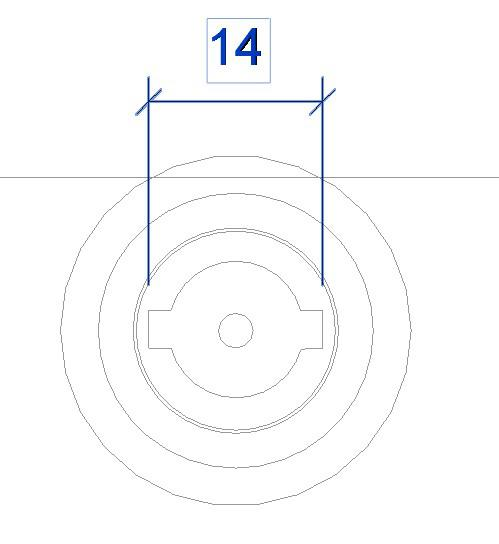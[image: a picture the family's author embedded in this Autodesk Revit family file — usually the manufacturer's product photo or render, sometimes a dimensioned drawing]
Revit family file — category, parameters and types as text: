
# Revit family: AquaMaster-Inverter-P_RFA-2022
name_source: partatom
category: Mechanické zařízení
units: mm (PartAtom-declared; Revit-internal decimal feet)

## family parameters
Bod výpočtu místnosti = Ne
Kóta kulaté spojky = Použít průměr
Nadpis OmniClass = Climate Control (HVAC)
Ořezat dutým tvarem při načtení = Ne
Sdílené = Ne
Typ dílu = Normální
Vždy vertikální = Ano
Zachovat orientaci poznámky = Ne
Založené na pracovní rovině = Ne
Číslo OmniClass = 23.75.00.00

## types (5) — shared parameters
CI_otopná voda – vstup = 1'' (vnější)
CO_otopná voda – výstup = 1'' (vnější)
MT_CI diameter = 28 mm  [stored 0.0918635 ft]
MT_CO diameter = 28 mm  [stored 0.0918635 ft]
MT_EC1 offset_X = 25 mm  [stored 0.082021 ft]
MT_active power = 0 W
MT_angle length_X = 406 mm  [stored 1.33202 ft]
MT_angle offset = 60 mm  [stored 0.19685 ft]
MT_apparent power = 0 VA
MT_case mat = MT_RAL7016
MT_case width = 526 mm  [stored 1.72572 ft]
MT_clearance back = 200 mm  [stored 0.656168 ft]
MT_clearance front = 600 mm
MT_cover front_X = 446 mm  [stored 1.46325 ft]
MT_cover top_X = 446 mm  [stored 1.46325 ft]
MT_frekvence (Hz) = 50 Hz
MT_ground height = 30 mm  [stored 0.0984252 ft]
MT_pipe connector mat = MT_RGB-130-130-130
MT_pipe mat = MT_angle-corner
Popis = Tepelné čerpadlo země/voda (R290)
URL = https://www.mastertherm.cz
Výrobce = Master Therm
zero-valued in all types: Cena, MT_CosPhi, Výchozí výška

## per-type parameters (varying)
- AQ45IP: EI_kolektor – vstup=5/4'' (vnější); EO_kolektor – výstup=5/4'' (vnější); Elektropřipojení=2xPG16; 4xPG13.5; Komentáře k typům=KOMPRESOR: BLDC Inverter; 15 – 120 rps; olej – (HAF68D1U) – 2.0 l; max. prov. proud – 24 A; VÝPARNÍK: deskový (nerez.); AISI316; průtok vody (W/W) – 2.14 kg/s; min. průtok – 1.61 kg/s; průtok směsi (B/W) – 1.04 kg/s; min. průtok – 0.63 kg/s; teplotní rozdíl – 3 K; vnitřní objem – 5.1 l; ext. tlak čerpadla – 15 m; max. příkon čerpadla – 400 W; KONDENZÁTOR: deskový (nerez.); AISI316; průtok otopné vody – 0.7 kg/s; min. průtok – 0.53 kg/s; teplotní rozdíl – 5 K; vnitřní objem – 4.1 l; ext. tlak čerpadla – 8.0 m; max. příkon čerpadla – 200 W; CHL. OKRUH: R290 (0.9 kg); EK (volitelně): není k dispozici; REGULACE: regulátor – pCO5; EEV – ano; čidlo otopné vody – ano; čidlo mix – ano (2x); čidlo TUV – ano; ext. čidlo – ano; ekviterm. reg. – ano; chladivo – 2xPT; ESI: 3x400 V; 50 Hz; max. proud – 25 A; ROZMĚRY: otopná voda, směs – 1", 5/4" (vnější); 120x53x72 cm; 180 kg; LIMITNÍ PROVOZNÍ PARAMETRY: max. přetlak vody – 0.25 MPa; max. přetlak chladiva – 3.1 MPa; směs min./max.: -5/+20 °C; voda min./max.: 20/75 °C; MT_CI offset_X=73 mm  [stored 0.239501 ft]; MT_CO offset_X=173 mm  [stored 0.567585 ft]; MT_EC1 offset_Y=90 mm; MT_EC2 offset_X=25 mm  [stored 0.082021 ft]; MT_EC2 offset_Y=60 mm  [stored 0.19685 ft]; MT_EC3 offset_X=25 mm  [stored 0.082021 ft]; MT_EC3 offset_Y=30 mm  [stored 0.0984252 ft]; MT_EC4 offset_X=421 mm  [stored 1.38123 ft]; MT_EC4 offset_Y=90 mm; MT_EC5 offset_X=421 mm  [stored 1.38123 ft]; MT_EC5 offset_Y=60 mm  [stored 0.19685 ft]; MT_EC5-EC6_YES=Ano; MT_EC6 offset_X=421 mm  [stored 1.38123 ft]; MT_EC6 offset_Y=30 mm  [stored 0.0984252 ft]; MT_EI diameter=35 mm  [stored 0.114829 ft]; MT_EI offset_X=373 mm  [stored 1.22375 ft]; MT_EO diameter=35 mm  [stored 0.114829 ft]; MT_EO offset_X=273 mm  [stored 0.895669 ft]; MT_TYPE=45; MT_angle length_Y=596 mm  [stored 1.95538 ft]; MT_angle length_Z=1080 mm  [stored 3.54331 ft]; MT_case depth=716 mm  [stored 2.34908 ft]; MT_case height=1200 mm; MT_center lock_YES=Ne; MT_clearance left=400 mm  [stored 1.31234 ft]; MT_clearance right=400 mm  [stored 1.31234 ft]; MT_clearance top=1800 mm  [stored 5.90551 ft]; MT_cover front_Y=1120 mm  [stored 3.67454 ft]; MT_cover side_X=636 mm  [stored 2.08661 ft]; MT_cover side_Y=1120 mm  [stored 3.67454 ft]; MT_cover top_Y=636 mm  [stored 2.08661 ft]; MT_hmotnost (kg)=180; MT_max. proud, vč. EK (A)=25 A; MT_napětí (V)=400 V; MT_pipe connector angle=0.00°; MT_pipe connector offset=486 mm; MT_pipe connector_X=446 mm  [stored 1.46325 ft]; MT_pipe connector_Y=120 mm  [stored 0.393701 ft]; MT_pivot offset=0 mm  [stored 0 ft]; MT_vent grille_YES=Ne; Model=AquaMaster 45 Inverter P
- AQ17IP: EI_kolektor – vstup=1'' (vnější); EO_kolektor – výstup=1'' (vnější); Elektropřipojení=4xPG16; Komentáře k typům=KOMPRESOR: BLDC Inverter; 20 – 60 rps; olej – (RFL68EP) – 0.74 l; max. prov. proud – 12 A; VÝPARNÍK: deskový (nerez.); AISI316; průtok vody (W/W) – 0.22 kg/s; min. průtok – 0.17 kg/s; průtok směsi (B/W) – 0.18 kg/s; min. průtok – 0.11 kg/s; teplotní rozdíl – 3 K; vnitřní objem – 2.0 l; ext. tlak čerpadla – 6.0 m; max. příkon čerpadla – 70 W; KONDENZÁTOR: deskový (nerez.); AISI316; průtok otopné vody – 0.12 kg/s; min. průtok – 0.06 kg/s; teplotní rozdíl – 5 K; vnitřní objem – 2.0 l; ext. tlak čerpadla – 5.0 m; max. příkon čerpadla – 70 W; CHL. OKRUH: R290 (0.152 kg); EK (volitelně): není k dispozici; REGULACE: regulátor – pCO5; EEV – ano; čidlo otopné vody – ano; čidlo mix – ano (2x); čidlo TUV – ano; ext. čidlo – ano; ekviterm. reg. – ano; chladivo – 2xPT; ESI: 1x230 V; 50 Hz; max. proud – 16 A; ROZMĚRY: otopná voda, směs – 1", 1" (vnější); 84x53x53 cm; 75 kg; LIMITNÍ PROVOZNÍ PARAMETRY: max. přetlak vody – 0.25 MPa; max. přetlak chladiva – 3.1 MPa; směs min./max.: -5/+20 °C; voda min./max.: 20/75 °C; MT_CI offset_X=430 mm; MT_CO offset_X=700 mm  [stored 2.29659 ft]; MT_EC1 offset_Y=500 mm  [stored 1.64042 ft]; MT_EC2 offset_X=55 mm  [stored 0.180446 ft]; MT_EC2 offset_Y=500 mm  [stored 1.64042 ft]; MT_EC3 offset_X=85 mm  [stored 0.278871 ft]; MT_EC3 offset_Y=500 mm  [stored 1.64042 ft]; MT_EC4 offset_X=115 mm; MT_EC4 offset_Y=500 mm  [stored 1.64042 ft]; MT_EC5 offset_X=115 mm; MT_EC5 offset_Y=500 mm  [stored 1.64042 ft]; MT_EC5-EC6_YES=Ne; MT_EC6 offset_X=115 mm; MT_EC6 offset_Y=500 mm  [stored 1.64042 ft]; MT_EI diameter=28 mm  [stored 0.0918635 ft]; MT_EI offset_X=330 mm  [stored 1.08268 ft]; MT_EO diameter=28 mm  [stored 0.0918635 ft]; MT_EO offset_X=60 mm  [stored 0.19685 ft]; MT_TYPE=17; MT_angle length_Y=406 mm  [stored 1.33202 ft]; MT_angle length_Z=720 mm  [stored 2.3622 ft]; MT_case depth=526 mm  [stored 1.72572 ft]; MT_case height=840 mm  [stored 2.75591 ft]; MT_center lock_YES=Ano; MT_clearance left=200 mm  [stored 0.656168 ft]; MT_clearance right=600 mm; MT_clearance top=1440 mm  [stored 4.72441 ft]; MT_cover front_Y=760 mm  [stored 2.49344 ft]; MT_cover side_X=446 mm  [stored 1.46325 ft]; MT_cover side_Y=760 mm  [stored 2.49344 ft]; MT_cover top_Y=446 mm  [stored 1.46325 ft]; MT_hmotnost (kg)=75; MT_max. proud, vč. EK (A)=16 A; MT_napětí (V)=230 V; MT_pipe connector angle=90.00°; MT_pipe connector offset=800 mm; MT_pipe connector_X=760 mm  [stored 2.49344 ft]; MT_pipe connector_Y=85 mm  [stored 0.278871 ft]; MT_pivot offset=526 mm  [stored 1.72572 ft]; MT_vent grille_YES=Ano; Model=AquaMaster 17 Inverter P
- AQ22IP: EI_kolektor – vstup=1'' (vnější); EO_kolektor – výstup=1'' (vnější); Elektropřipojení=4xPG16; Komentáře k typům=KOMPRESOR: BLDC Inverter; 20 – 90 rps; olej – (RFL68EP) – 0.74 l; max. prov. proud – 12 A; VÝPARNÍK: deskový (nerez.); AISI316; průtok vody (W/W) – 0.46 kg/s; min. průtok – 0.35 kg/s; průtok směsi (B/W) – 0.36 kg/s; min. průtok – 0.21 kg/s; teplotní rozdíl – 3 K; vnitřní objem – 2.0 l; ext. tlak čerpadla – 4.5 m; max. příkon čerpadla – 70 W; KONDENZÁTOR: deskový (nerez.); AISI316; průtok otopné vody – 0.25 kg/s; min. průtok – 0.13 kg/s; teplotní rozdíl – 5 K; vnitřní objem – 2.0 l; ext. tlak čerpadla – 7.0 m; max. příkon čerpadla – 70 W; CHL. OKRUH: R290 (0.220 kg); EK (volitelně): není k dispozici; REGULACE: regulátor – pCO5; EEV – ano; čidlo otopné vody – ano; čidlo mix – ano (2x); čidlo TUV – ano; ext. čidlo – ano; ekviterm. reg. – ano; chladivo – 2xPT; ESI: 1x230 V; 50 Hz; max. proud – 20 A; ROZMĚRY: otopná voda, směs – 1", 1" (vnější); 84x53x53 cm; 80 kg; LIMITNÍ PROVOZNÍ PARAMETRY: max. přetlak vody – 0.25 MPa; max. přetlak chladiva – 3.1 MPa; směs min./max.: -5/+20 °C; voda min./max.: 20/75 °C; MT_CI offset_X=430 mm; MT_CO offset_X=700 mm  [stored 2.29659 ft]; MT_EC1 offset_Y=500 mm  [stored 1.64042 ft]; MT_EC2 offset_X=55 mm  [stored 0.180446 ft]; MT_EC2 offset_Y=500 mm  [stored 1.64042 ft]; MT_EC3 offset_X=85 mm  [stored 0.278871 ft]; MT_EC3 offset_Y=500 mm  [stored 1.64042 ft]; MT_EC4 offset_X=115 mm; MT_EC4 offset_Y=500 mm  [stored 1.64042 ft]; MT_EC5 offset_X=115 mm; MT_EC5 offset_Y=500 mm  [stored 1.64042 ft]; MT_EC5-EC6_YES=Ne; MT_EC6 offset_X=115 mm; MT_EC6 offset_Y=500 mm  [stored 1.64042 ft]; MT_EI diameter=28 mm  [stored 0.0918635 ft]; MT_EI offset_X=330 mm  [stored 1.08268 ft]; MT_EO diameter=28 mm  [stored 0.0918635 ft]; MT_EO offset_X=60 mm  [stored 0.19685 ft]; MT_TYPE=22; MT_angle length_Y=406 mm  [stored 1.33202 ft]; MT_angle length_Z=720 mm  [stored 2.3622 ft]; MT_case depth=526 mm  [stored 1.72572 ft]; MT_case height=840 mm  [stored 2.75591 ft]; MT_center lock_YES=Ano; MT_clearance left=200 mm  [stored 0.656168 ft]; MT_clearance right=600 mm; MT_clearance top=1440 mm  [stored 4.72441 ft]; MT_cover front_Y=760 mm  [stored 2.49344 ft]; MT_cover side_X=446 mm  [stored 1.46325 ft]; MT_cover side_Y=760 mm  [stored 2.49344 ft]; MT_cover top_Y=446 mm  [stored 1.46325 ft]; MT_hmotnost (kg)=80; MT_max. proud, vč. EK (A)=20 A; MT_napětí (V)=230 V; MT_pipe connector angle=90.00°; MT_pipe connector offset=800 mm; MT_pipe connector_X=760 mm  [stored 2.49344 ft]; MT_pipe connector_Y=85 mm  [stored 0.278871 ft]; MT_pivot offset=526 mm  [stored 1.72572 ft]; MT_vent grille_YES=Ano; Model=AquaMaster 22 Inverter P
- AQ30IP: EI_kolektor – vstup=1'' (vnější); EO_kolektor – výstup=1'' (vnější); Elektropřipojení=2xPG16; 4xPG13.5; Komentáře k typům=KOMPRESOR: BLDC Inverter; 15 – 110 rps; olej – (PZ68S) – 0.75 l; max. prov. proud – ; VÝPARNÍK: deskový (nerez.); AISI316; průtok vody (W/W) – 0.99 kg/s; min. průtok – 0.74 kg/s; průtok směsi (B/W) – 0.48 kg/s; min. průtok – 0.29 kg/s; teplotní rozdíl – 3 K; vnitřní objem – 3.8 l; ext. tlak čerpadla – 5.5 m; max. příkon čerpadla – 70 W; KONDENZÁTOR: deskový (nerez.); AISI316; průtok otopné vody – 0.37 kg/s; min. průtok – 0.25 kg/s; teplotní rozdíl – 5 K; vnitřní objem – 4.0 l; ext. tlak čerpadla – 6.5 m; max. příkon čerpadla – 70 W; CHL. OKRUH: R290 (0.7 kg); EK (volitelně): není k dispozici; REGULACE: regulátor – pCO5; EEV – ano; čidlo otopné vody – ano; čidlo mix – ano (2x); čidlo TUV – ano; ext. čidlo – ano; ekviterm. reg. – ano; chladivo – 2xPT; ESI: 1x230 V; 50 Hz; max. proud – 25 A; ROZMĚRY: otopná voda, směs – 1", 1" (vnější); 120x56x72 cm; 165 kg; LIMITNÍ PROVOZNÍ PARAMETRY: max. přetlak vody – 0.25 MPa; max. přetlak chladiva – 2.9 MPa; směs min./max.: -5/+20 °C; voda min./max.: 20/75 °C; MT_CI offset_X=73 mm  [stored 0.239501 ft]; MT_CO offset_X=173 mm  [stored 0.567585 ft]; MT_EC1 offset_Y=90 mm; MT_EC2 offset_X=25 mm  [stored 0.082021 ft]; MT_EC2 offset_Y=60 mm  [stored 0.19685 ft]; MT_EC3 offset_X=25 mm  [stored 0.082021 ft]; MT_EC3 offset_Y=30 mm  [stored 0.0984252 ft]; MT_EC4 offset_X=421 mm  [stored 1.38123 ft]; MT_EC4 offset_Y=90 mm; MT_EC5 offset_X=421 mm  [stored 1.38123 ft]; MT_EC5 offset_Y=60 mm  [stored 0.19685 ft]; MT_EC5-EC6_YES=Ano; MT_EC6 offset_X=421 mm  [stored 1.38123 ft]; MT_EC6 offset_Y=30 mm  [stored 0.0984252 ft]; MT_EI diameter=28 mm  [stored 0.0918635 ft]; MT_EI offset_X=373 mm  [stored 1.22375 ft]; MT_EO diameter=28 mm  [stored 0.0918635 ft]; MT_EO offset_X=273 mm  [stored 0.895669 ft]; MT_TYPE=30; MT_angle length_Y=596 mm  [stored 1.95538 ft]; MT_angle length_Z=1080 mm  [stored 3.54331 ft]; MT_case depth=716 mm  [stored 2.34908 ft]; MT_case height=1200 mm; MT_center lock_YES=Ne; MT_clearance left=400 mm  [stored 1.31234 ft]; MT_clearance right=400 mm  [stored 1.31234 ft]; MT_clearance top=1800 mm  [stored 5.90551 ft]; MT_cover front_Y=1120 mm  [stored 3.67454 ft]; MT_cover side_X=636 mm  [stored 2.08661 ft]; MT_cover side_Y=1120 mm  [stored 3.67454 ft]; MT_cover top_Y=636 mm  [stored 2.08661 ft]; MT_hmotnost (kg)=165; MT_max. proud, vč. EK (A)=25 A; MT_napětí (V)=230 V; MT_pipe connector angle=0.00°; MT_pipe connector offset=486 mm; MT_pipe connector_X=446 mm  [stored 1.46325 ft]; MT_pipe connector_Y=120 mm  [stored 0.393701 ft]; MT_pivot offset=0 mm  [stored 0 ft]; MT_vent grille_YES=Ne; Model=AquaMaster 30 Inverter P
- AQ37IP: EI_kolektor – vstup=1'' (vnější); EO_kolektor – výstup=1'' (vnější); Elektropřipojení=2xPG16; 4xPG13.5; Komentáře k typům=KOMPRESOR: BLDC Inverter; 15 – 100 rps; olej – (PZ68S) – 0.9 l; max. prov. proud – ; VÝPARNÍK: deskový (nerez.); AISI316; průtok vody (W/W) – 1.54 kg/s; min. průtok – 1.16 kg/s; průtok směsi (B/W) – 0.77 kg/s; min. průtok – 0.46 kg/s; teplotní rozdíl – 3 K; vnitřní objem – 3.8 l; ext. tlak čerpadla – 7.5 m; max. příkon čerpadla – 200 W; KONDENZÁTOR: deskový (nerez.); AISI316; průtok otopné vody – 0.6 kg/s; min. průtok – 0.4 kg/s; teplotní rozdíl – 5 K; vnitřní objem – 4.0 l; ext. tlak čerpadla – 4.5 m; max. příkon čerpadla – 70 W; CHL. OKRUH: R290 (0.9 kg); EK (volitelně): není k dispozici; REGULACE: regulátor – pCO5; EEV – ano; čidlo otopné vody – ano; čidlo mix – ano (2x); čidlo TUV – ano; ext. čidlo – ano; ekviterm. reg. – ano; chladivo – 2xPT; ESI: 3x400 V; 50 Hz; max. proud – 20 A; ROZMĚRY: otopná voda, směs – 1", 1" (vnější); 120x56x72 cm; 180 kg; LIMITNÍ PROVOZNÍ PARAMETRY: max. přetlak vody – 0.25 MPa; max. přetlak chladiva – 2.9 MPa; směs min./max.: -5/+20 °C; voda min./max.: 20/75 °C; MT_CI offset_X=73 mm  [stored 0.239501 ft]; MT_CO offset_X=173 mm  [stored 0.567585 ft]; MT_EC1 offset_Y=90 mm; MT_EC2 offset_X=25 mm  [stored 0.082021 ft]; MT_EC2 offset_Y=60 mm  [stored 0.19685 ft]; MT_EC3 offset_X=25 mm  [stored 0.082021 ft]; MT_EC3 offset_Y=30 mm  [stored 0.0984252 ft]; MT_EC4 offset_X=421 mm  [stored 1.38123 ft]; MT_EC4 offset_Y=90 mm; MT_EC5 offset_X=421 mm  [stored 1.38123 ft]; MT_EC5 offset_Y=60 mm  [stored 0.19685 ft]; MT_EC5-EC6_YES=Ano; MT_EC6 offset_X=421 mm  [stored 1.38123 ft]; MT_EC6 offset_Y=30 mm  [stored 0.0984252 ft]; MT_EI diameter=28 mm  [stored 0.0918635 ft]; MT_EI offset_X=373 mm  [stored 1.22375 ft]; MT_EO diameter=28 mm  [stored 0.0918635 ft]; MT_EO offset_X=273 mm  [stored 0.895669 ft]; MT_TYPE=37; MT_angle length_Y=596 mm  [stored 1.95538 ft]; MT_angle length_Z=1080 mm  [stored 3.54331 ft]; MT_case depth=716 mm  [stored 2.34908 ft]; MT_case height=1200 mm; MT_center lock_YES=Ne; MT_clearance left=400 mm  [stored 1.31234 ft]; MT_clearance right=400 mm  [stored 1.31234 ft]; MT_clearance top=1800 mm  [stored 5.90551 ft]; MT_cover front_Y=1120 mm  [stored 3.67454 ft]; MT_cover side_X=636 mm  [stored 2.08661 ft]; MT_cover side_Y=1120 mm  [stored 3.67454 ft]; MT_cover top_Y=636 mm  [stored 2.08661 ft]; MT_hmotnost (kg)=180; MT_max. proud, vč. EK (A)=20 A; MT_napětí (V)=400 V; MT_pipe connector angle=0.00°; MT_pipe connector offset=486 mm; MT_pipe connector_X=446 mm  [stored 1.46325 ft]; MT_pipe connector_Y=120 mm  [stored 0.393701 ft]; MT_pivot offset=0 mm  [stored 0 ft]; MT_vent grille_YES=Ne; Model=AquaMaster 37 Inverter P

note: [stored X ft] marks values corroborated as IEEE doubles in the binary element streams (Revit-internal decimal feet)
